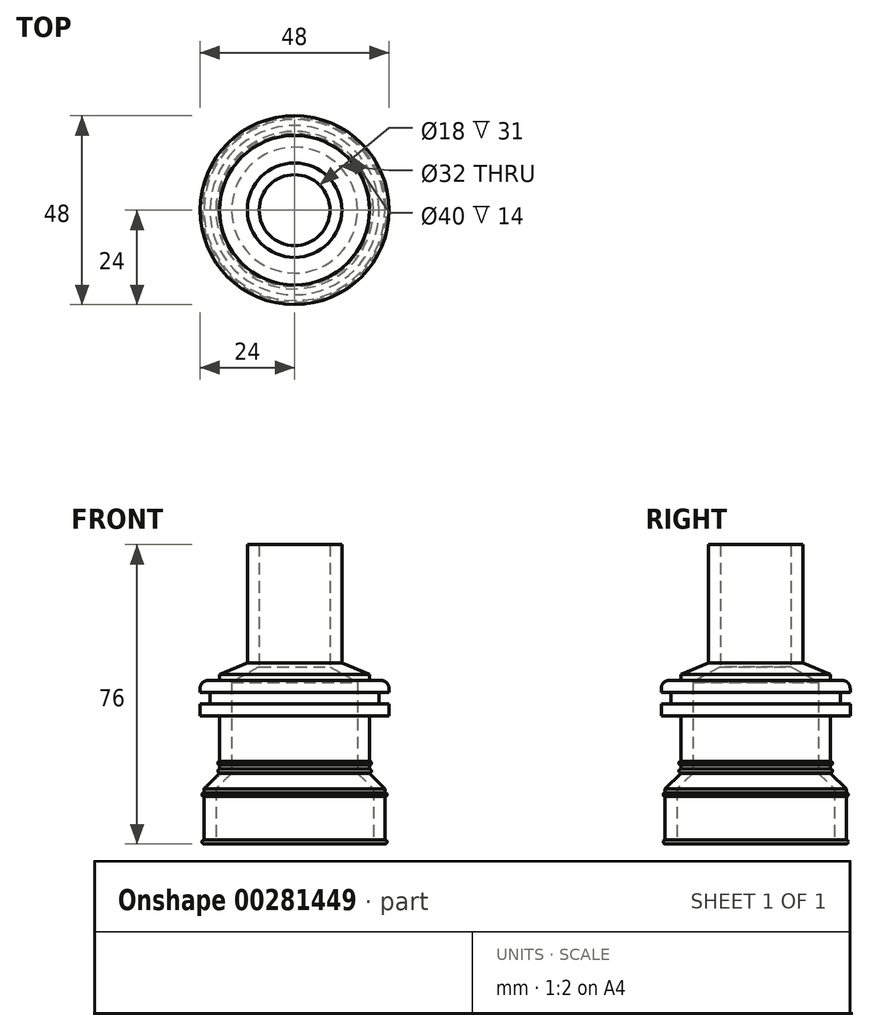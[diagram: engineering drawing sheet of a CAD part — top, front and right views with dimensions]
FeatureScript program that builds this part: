
annotation { "Feature Type Name" : "Feature", "Feature Type Description" : "" }
export const myFeature = defineFeature(function(context is Context, id is Id, definition is map)
    precondition{}
    {
        {
            var Q0;
            Q0=qCreatedBy(makeId("Front.planeOp"),FACE);
            var sketch = newSketch(context, id + "F0", { "sketchPlane" : qUnion([Q0])});
            skLineSegment(sketch, "E0", {"start": v(23.5, 0.5) * mm, "end": v(23.5, 0.5) * mm});
            skLineSegment(sketch, "E1", {"start": v(23, 1) * mm, "end": v(23, 1) * mm});
            skLineSegment(sketch, "E2", {"start": v(23, 1) * mm, "end": v(23, 12) * mm});
            skLineSegment(sketch, "E3", {"start": v(23, 12) * mm, "end": v(23, 12) * mm});
            skLineSegment(sketch, "E4", {"start": v(23.5, 12.5) * mm, "end": v(23.5, 12.5) * mm});
            skLineSegment(sketch, "E5", {"start": v(23, 13) * mm, "end": v(23, 13) * mm});
            skLineSegment(sketch, "E6", {"start": v(23, 13) * mm, "end": v(23, 14) * mm});
            skLineSegment(sketch, "E7", {"start": v(23, 14) * mm, "end": v(19, 17.9) * mm});
            skLineSegment(sketch, "E8", {"start": v(19, 17.9) * mm, "end": v(19, 18) * mm});
            skLineSegment(sketch, "E9", {"start": v(19, 18) * mm, "end": v(19, 18) * mm});
            skLineSegment(sketch, "E10", {"start": v(19.5, 18.5) * mm, "end": v(19.5, 18.5) * mm});
            skLineSegment(sketch, "E11", {"start": v(19, 19) * mm, "end": v(19, 19) * mm});
            skLineSegment(sketch, "E12", {"start": v(19, 19) * mm, "end": v(19, 20) * mm});
            skLineSegment(sketch, "E13", {"start": v(19, 20) * mm, "end": v(19, 20) * mm});
            skLineSegment(sketch, "E14", {"start": v(19.5, 20.5) * mm, "end": v(19.5, 20.5) * mm});
            skLineSegment(sketch, "E15", {"start": v(19, 21) * mm, "end": v(19, 21) * mm});
            skLineSegment(sketch, "E16", {"start": v(19, 21) * mm, "end": v(19, 32.5) * mm});
            skLineSegment(sketch, "E17", {"start": v(19, 32.5) * mm, "end": v(24, 32.5) * mm});
            skLineSegment(sketch, "E18", {"start": v(24, 32.5) * mm, "end": v(24, 35.5) * mm});
            skLineSegment(sketch, "E19", {"start": v(24, 35.5) * mm, "end": v(21.5, 35.5) * mm});
            skLineSegment(sketch, "E20", {"start": v(21.5, 35.5) * mm, "end": v(21.5, 38.5) * mm});
            skLineSegment(sketch, "E21", {"start": v(21.5, 38.5) * mm, "end": v(24, 38.5) * mm});
            skLineSegment(sketch, "E22", {"start": v(24, 38.5) * mm, "end": v(24, 39.5) * mm});
            skLineSegment(sketch, "E23", {"start": v(22, 41.5) * mm, "end": v(19, 41.5) * mm});
            skLineSegment(sketch, "E24", {"start": v(19, 41.5) * mm, "end": v(19, 43) * mm});
            skLineSegment(sketch, "E25", {"start": v(19, 43) * mm, "end": v(12, 46) * mm});
            skLineSegment(sketch, "E26", {"start": v(12, 46) * mm, "end": v(12, 76) * mm});
            skLineSegment(sketch, "E27", {"start": v(0, 0) * mm, "end": v(0, 82.25) * mm, "construction": true});
            skPoint(sketch, "E28.visualSharp", {"position": v(24, 41.5) * mm});
            skArc(sketch, "E28.filletArc", {"start": v(24, 39.5) * mm, "mid": v(23.41, 40.91) * mm, "end": v(22, 41.5) * mm});
            skPoint(sketch, "E29.visualSharp", {"position": v(19.5, 21) * mm});
            skArc(sketch, "E29.filletArc", {"start": v(19.5, 20.5) * mm, "mid": v(19.35, 20.85) * mm, "end": v(19, 21) * mm});
            skPoint(sketch, "E30.visualSharp", {"position": v(19.5, 20) * mm});
            skArc(sketch, "E30.filletArc", {"start": v(19, 20) * mm, "mid": v(19.35, 20.15) * mm, "end": v(19.5, 20.5) * mm});
            skPoint(sketch, "E31.visualSharp", {"position": v(19.5, 19) * mm});
            skArc(sketch, "E31.filletArc", {"start": v(19.5, 18.5) * mm, "mid": v(19.35, 18.85) * mm, "end": v(19, 19) * mm});
            skPoint(sketch, "E32.visualSharp", {"position": v(19.5, 18) * mm});
            skArc(sketch, "E32.filletArc", {"start": v(19, 18) * mm, "mid": v(19.35, 18.15) * mm, "end": v(19.5, 18.5) * mm});
            skPoint(sketch, "E33.visualSharp", {"position": v(23.5, 13) * mm});
            skArc(sketch, "E33.filletArc", {"start": v(23.5, 12.5) * mm, "mid": v(23.35, 12.85) * mm, "end": v(23, 13) * mm});
            skPoint(sketch, "E34.visualSharp", {"position": v(23.5, 12) * mm});
            skArc(sketch, "E34.filletArc", {"start": v(23, 12) * mm, "mid": v(23.35, 12.15) * mm, "end": v(23.5, 12.5) * mm});
            skPoint(sketch, "E35.visualSharp", {"position": v(23.5, 1) * mm});
            skArc(sketch, "E35.filletArc", {"start": v(23.5, 0.5) * mm, "mid": v(23.35, 0.85) * mm, "end": v(23, 1) * mm});
            skLineSegment(sketch, "E36", {"start": v(23, 0) * mm, "end": v(20, 0) * mm});
            skPoint(sketch, "E37.visualSharp", {"position": v(23.5, 0) * mm});
            skArc(sketch, "E37.filletArc", {"start": v(23, 0) * mm, "mid": v(23.35, 0.15) * mm, "end": v(23.5, 0.5) * mm});
            skLineSegment(sketch, "E38", {"start": v(20, 0) * mm, "end": v(20, 14) * mm});
            skLineSegment(sketch, "E39", {"start": v(20, 14) * mm, "end": v(16, 17.9) * mm});
            skLineSegment(sketch, "E40", {"start": v(12, 76) * mm, "end": v(9, 76) * mm});
            skLineSegment(sketch, "E41", {"start": v(9, 76) * mm, "end": v(9, 45) * mm});
            skLineSegment(sketch, "E42", {"start": v(16, 41) * mm, "end": v(16, 17.9) * mm});
            skLineSegment(sketch, "E43", {"start": v(16, 41) * mm, "end": v(9, 45) * mm});
            skSolve(sketch);
        }
        {
            var Q0;
            Q0=qCreatedBy(makeId("Top.planeOp"),FACE);
            var sketch = newSketch(context, id + "F1", { "sketchPlane" : qUnion([Q0])});
            skCircle(sketch, "E44", {"center": v(0, 0) * mm, "radius": 20 * mm});
            skSolve(sketch);
        }
        {
            var Q0;
            Q0=makeQuery(id+"F0.imprint","IMPRINT",FACE,{"disambiguationData":[TD([[makeQuery(id+"F0.imprint","IMPRINT",EDGE,{"derivedFrom":sQuery(id+"F0.wireOp",EDGE,"E2")}),1.0]])]});
            var Q1;
            Q1=sQuery(id+"F1.wireOp",EDGE,"E44");
            revolve(context, id + "F2", {"entities" : qUnion([Q0]), "axis" : qUnion([Q1]), "revolveType" : RevolveType.FULL});
        }
    });
